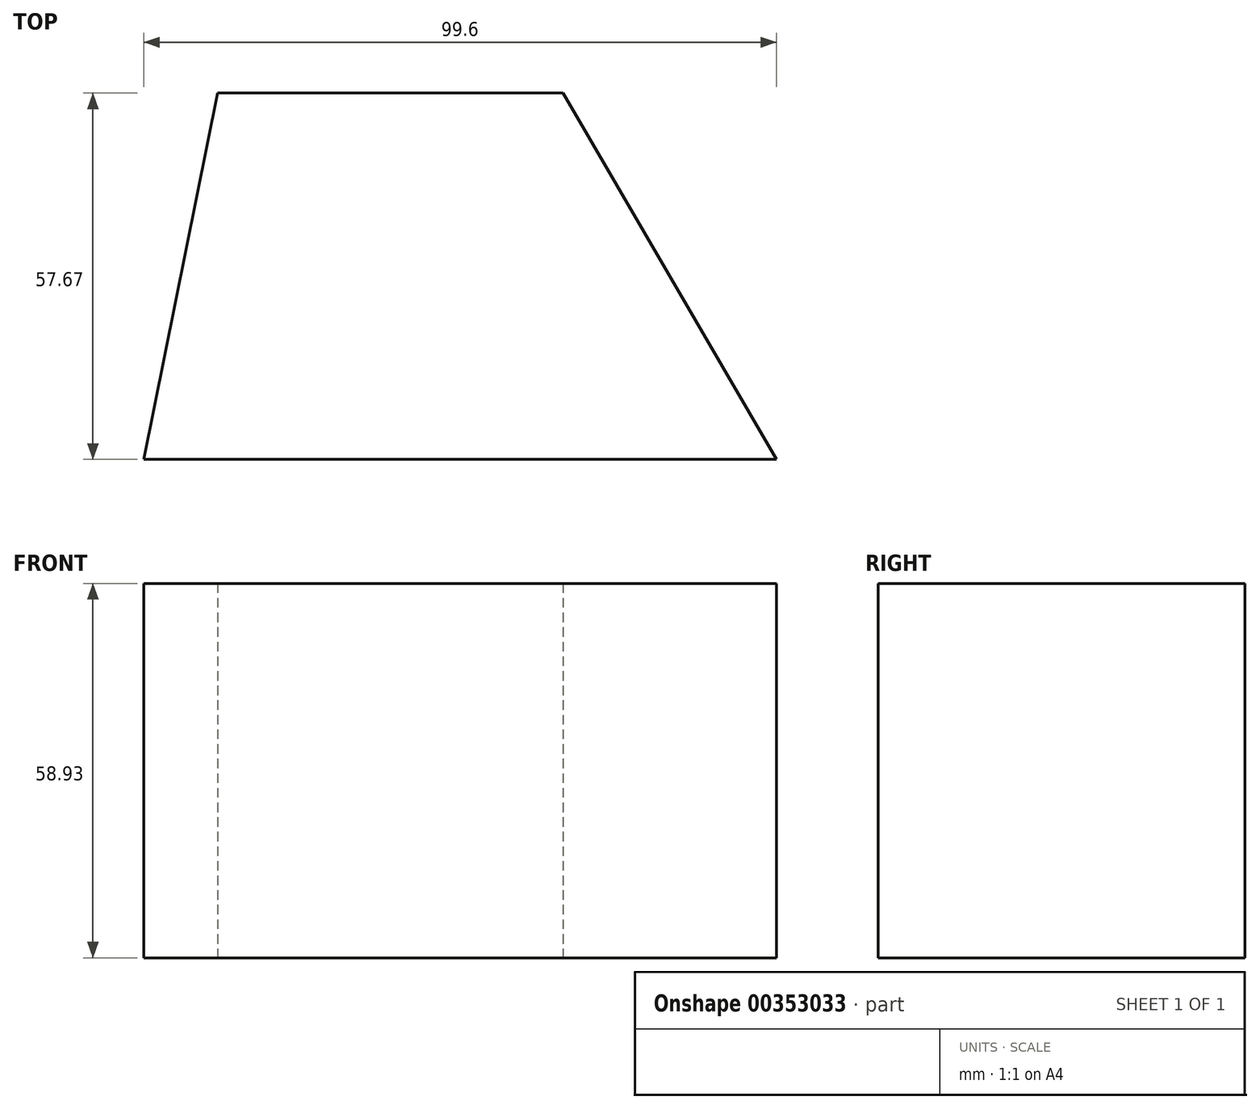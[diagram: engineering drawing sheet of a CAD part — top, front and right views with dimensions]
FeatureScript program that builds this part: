
annotation { "Feature Type Name" : "Feature", "Feature Type Description" : "" }
export const myFeature = defineFeature(function(context is Context, id is Id, definition is map)
    precondition{}
    {
        {
            var Q0;
            Q0=qCreatedBy(makeId("Top.planeOp"),FACE);
            var sketch = newSketch(context, id + "F0", { "sketchPlane" : qUnion([Q0])});
            skLineSegment(sketch, "E0", {"start": v(-46.76, 0) * mm, "end": v(52.84, 0) * mm});
            skLineSegment(sketch, "E1", {"start": v(52.84, 0) * mm, "end": v(19.23, 57.67) * mm});
            skLineSegment(sketch, "E2", {"start": v(19.23, 57.67) * mm, "end": v(-35.14, 57.67) * mm});
            skLineSegment(sketch, "E3", {"start": v(-35.14, 57.67) * mm, "end": v(-46.76, 0) * mm});
            skSolve(sketch);
        }
        {
            var Q0;
            Q0=makeQuery(id+"F0.imprint","IMPRINT",FACE,{"disambiguationData":[TD([[makeQuery(id+"F0.imprint","IMPRINT",EDGE,{"derivedFrom":sQuery(id+"F0.wireOp",EDGE,"E0")}),1.0]])]});
            extrude(context, id + "F1", {"entities" : qUnion([Q0]), "depth" : 58.93 * mm});
        }
    });
